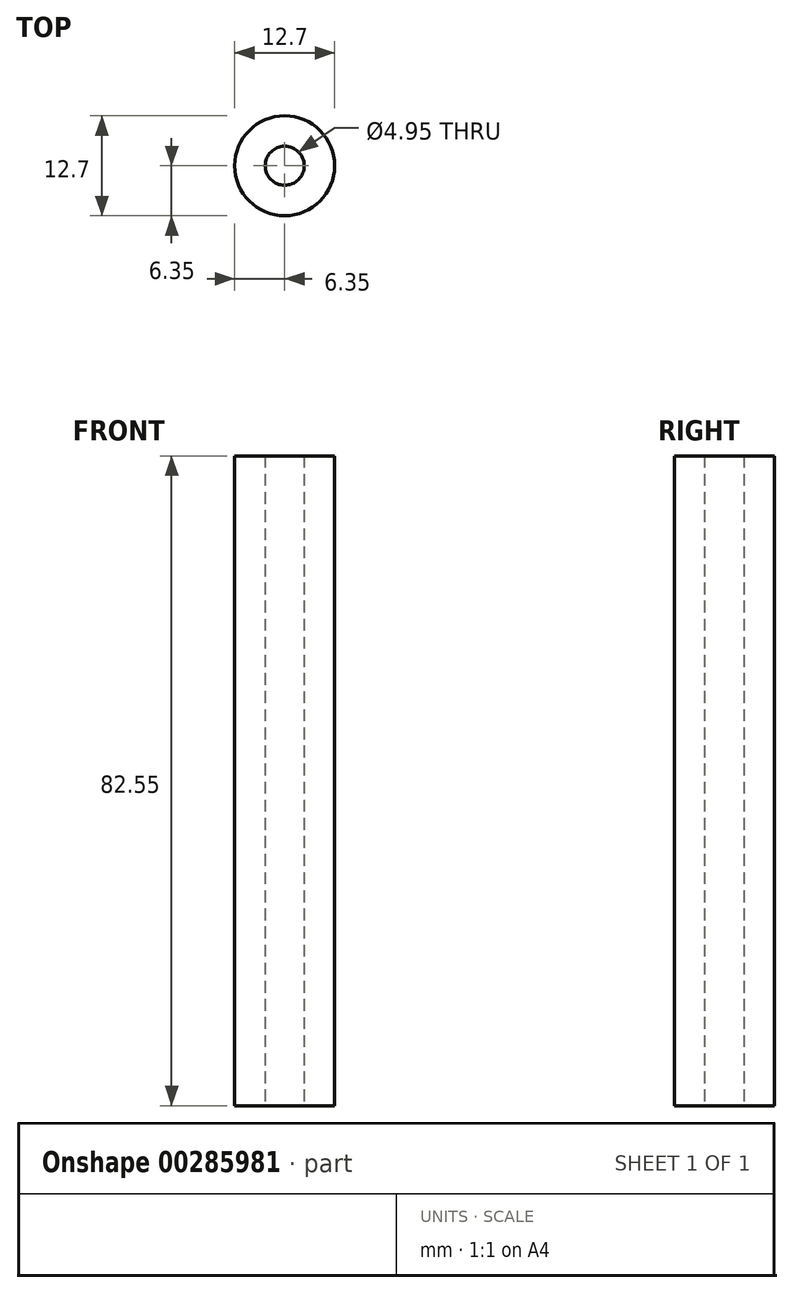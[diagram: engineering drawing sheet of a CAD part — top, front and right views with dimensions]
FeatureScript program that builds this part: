
annotation { "Feature Type Name" : "Feature", "Feature Type Description" : "" }
export const myFeature = defineFeature(function(context is Context, id is Id, definition is map)
    precondition{}
    {
        {
            var Q0;
            Q0=qCreatedBy(makeId("Top.planeOp"),FACE);
            var sketch = newSketch(context, id + "F0", { "sketchPlane" : qUnion([Q0])});
            skCircle(sketch, "E0", {"center": v(0, 0) * mm, "radius": 2.48 * mm});
            skCircle(sketch, "E1", {"center": v(0, 0) * mm, "radius": 6.35 * mm});
            skSolve(sketch);
        }
        {
            var Q0;
            Q0 = qSketchRegion(id + "F0", true);
            extrude(context, id + "F1", {"entities" : qUnion([Q0]), "depth" : 82.55 * mm});
        }
    });
